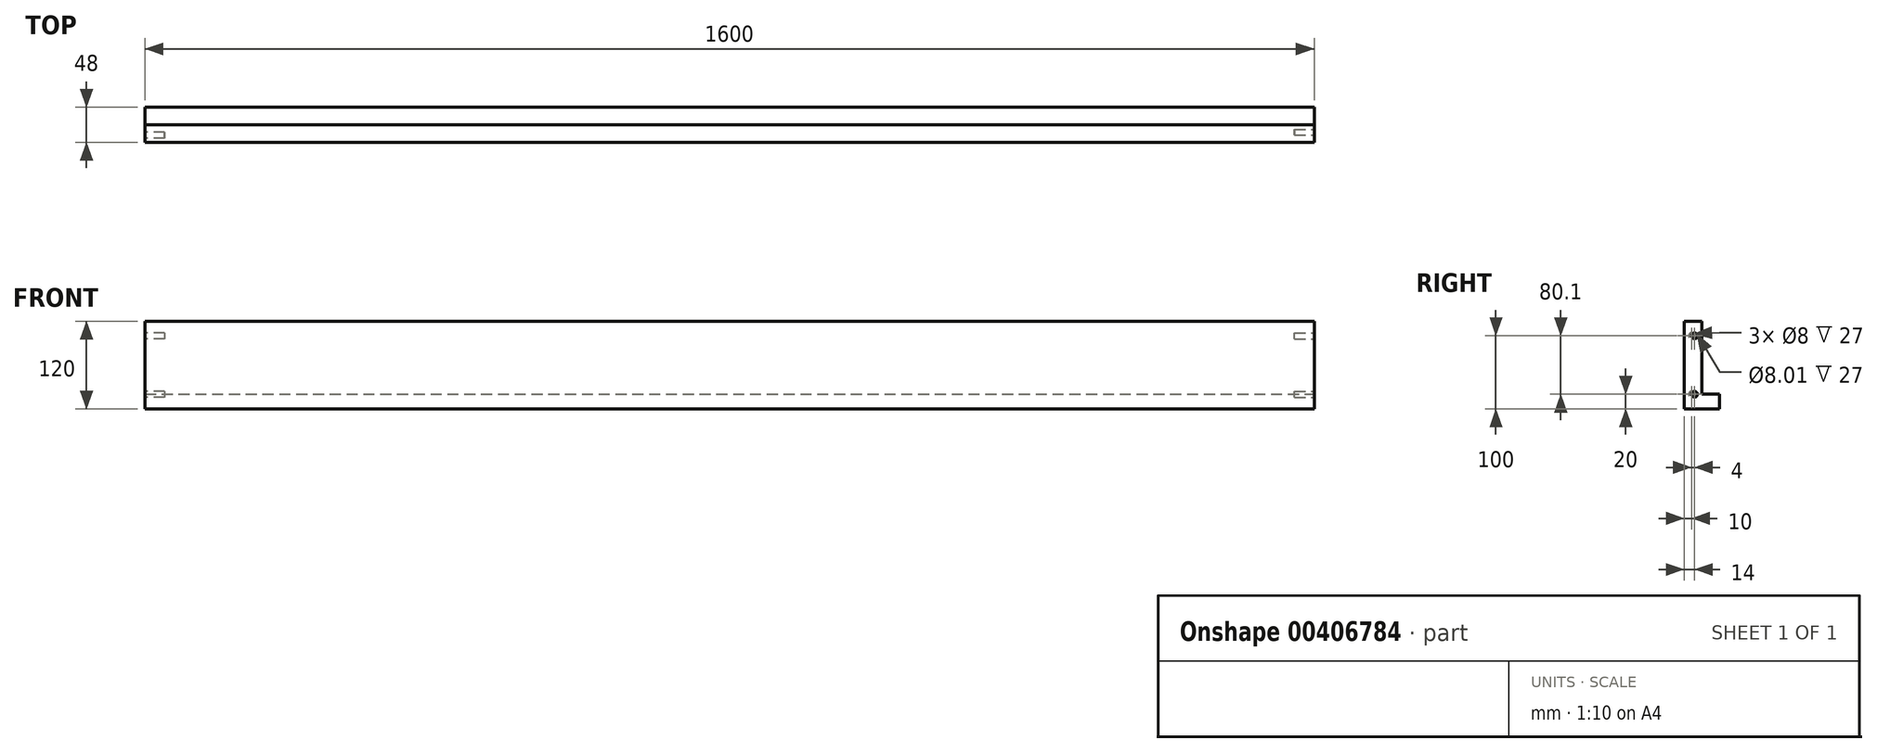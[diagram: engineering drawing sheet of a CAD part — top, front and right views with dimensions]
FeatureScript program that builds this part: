
annotation { "Feature Type Name" : "Feature", "Feature Type Description" : "" }
export const myFeature = defineFeature(function(context is Context, id is Id, definition is map)
    precondition{}
    {
        {
            var Q0;
            Q0=qCreatedBy(makeId("Front.planeOp"),FACE);
            var sketch = newSketch(context, id + "F0", { "sketchPlane" : qUnion([Q0])});
            skLineSegment(sketch, "E0.bottom", {"start": v(800, 60) * mm, "end": v(-800, 60) * mm});
            skLineSegment(sketch, "E0.top", {"start": v(800, -60) * mm, "end": v(-800, -60) * mm});
            skLineSegment(sketch, "E0.left", {"start": v(800, 60) * mm, "end": v(800, -60) * mm});
            skLineSegment(sketch, "E0.right", {"start": v(-800, 60) * mm, "end": v(-800, -60) * mm});
            skPoint(sketch, "E0.middle", {"position": v(0, 0) * mm});
            skSolve(sketch);
        }
        {
            var Q0;
            Q0 = qSketchRegion(id + "F0", true);
            extrude(context, id + "F1", {"entities" : qUnion([Q0]), "depth" : 24 * mm});
        }
        {
            var Q0;
            Q0=makeQuery(id+"F1.opExtrude","SWEPT_FACE",FACE,{"disambiguationData":[OSD([sQuery(id+"F0.wireOp",EDGE,"E0.left")])]});
            var sketch = newSketch(context, id + "F2", { "sketchPlane" : qUnion([Q0])});
            skCircle(sketch, "E1", {"center": v(-10, 40) * mm, "radius": 4 * mm});
            skCircle(sketch, "E2", {"center": v(-10, -40) * mm, "radius": 4 * mm});
            skSolve(sketch);
        }
        {
            var Q0;
            Q0 = qSketchRegion(id + "F2", true);
            extrude(context, id + "F3", {"entities" : qUnion([Q0]), "operationType" : NewBodyOperationType.REMOVE, "oppositeDirection" : true, "depth" : 27 * mm});
        }
        {
            var Q0;
            Q0=makeQuery(id+"F1.opExtrude","SWEPT_FACE",FACE,{"disambiguationData":[OSD([sQuery(id+"F0.wireOp",EDGE,"E0.right")])]});
            var sketch = newSketch(context, id + "F4", { "sketchPlane" : qUnion([Q0])});
            skCircle(sketch, "E3", {"center": v(14, 40.1) * mm, "radius": 4 * mm});
            skCircle(sketch, "E4", {"center": v(14, -40) * mm, "radius": 4 * mm});
            skSolve(sketch);
        }
        {
            var Q0;
            Q0 = qSketchRegion(id + "F4", true);
            extrude(context, id + "F5", {"entities" : qUnion([Q0]), "operationType" : NewBodyOperationType.REMOVE, "oppositeDirection" : true, "depth" : 27 * mm});
        }
        {
            var Q0;
            Q0=makeQuery(id+"F1.opExtrude","CAP_FACE",FACE,{"disambiguationData":[OSD([sQuery(id+"F0.wireOp",EDGE,"E0.bottom"),sQuery(id+"F0.wireOp",EDGE,"E0.top"),sQuery(id+"F0.wireOp",EDGE,"E0.left"),sQuery(id+"F0.wireOp",EDGE,"E0.right")])],"isStart":true});
            var sketch = newSketch(context, id + "F6", { "sketchPlane" : qUnion([Q0])});
            skLineSegment(sketch, "E5.bottom", {"start": v(800, -60) * mm, "end": v(-800, -60) * mm});
            skLineSegment(sketch, "E5.top", {"start": v(800, -40) * mm, "end": v(-800, -40) * mm});
            skLineSegment(sketch, "E5.left", {"start": v(800, -60) * mm, "end": v(800, -40) * mm});
            skLineSegment(sketch, "E5.right", {"start": v(-800, -60) * mm, "end": v(-800, -40) * mm});
            skSolve(sketch);
        }
        {
            var Q0;
            Q0 = qSketchRegion(id + "F6", true);
            extrude(context, id + "F7", {"entities" : qUnion([Q0]), "operationType" : NewBodyOperationType.ADD, "depth" : 24 * mm});
        }
    });
